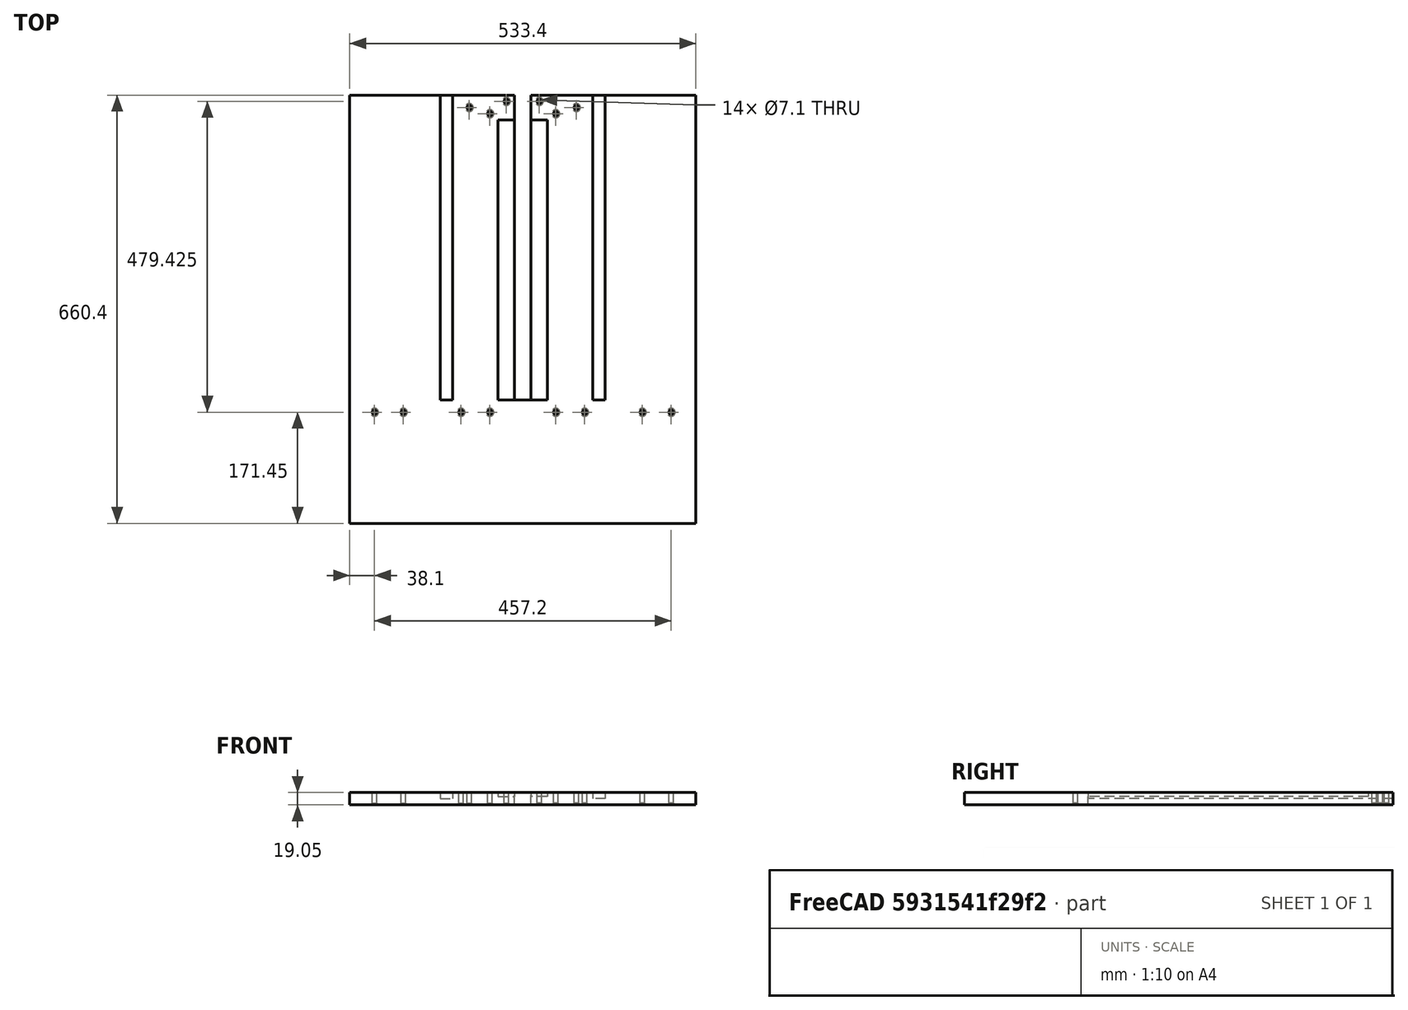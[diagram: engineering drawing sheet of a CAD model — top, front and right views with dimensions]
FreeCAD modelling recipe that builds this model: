
FCSTD DOCUMENT  (FreeCAD 0.20R29603 (Git))
Label: base
License: All rights reserved
LicenseURL: http://en.wikipedia.org/wiki/All_rights_reserved
objects: TechDraw::DrawViewDimension×20, Sketcher::SketchObject×4, PartDesign::Pocket×2, TechDraw::DrawViewPart×2, PartDesign::Pad×1, PartDesign::Hole×1, PartDesign::Mirrored×1, PartDesign::Body×1, TechDraw::DrawSVGTemplate×1, TechDraw::DrawPage×1
note: 14 computed .brp shape members not serialized (recipe doc carries the construction recipe); baked Part::Feature solids carry a one-line shape summary decoded from their .brp

FEATURE [Sketcher::SketchObject] Sketch
  FullyConstrained = true
  MapMode = 5
  Support = -> [XY_Plane]
  sketch-geometry (7):
    g0: LineSegment StartX=-127 StartY=-330.2 StartZ=0 EndX=-127 EndY=330.2 EndZ=0
    g1: LineSegment StartX=-127 StartY=330.2 StartZ=0 EndX=127 EndY=330.2 EndZ=0
    g2: LineSegment StartX=127 StartY=330.2 StartZ=0 EndX=127 EndY=-139.7 EndZ=0
    g3: GeomPoint X=0 Y=0 Z=0
    g4: LineSegment StartX=127 StartY=-139.7 StartZ=0 EndX=139.7 EndY=-139.7 EndZ=0
    g5: LineSegment StartX=139.7 StartY=-139.7 StartZ=0 EndX=139.7 EndY=-330.2 EndZ=0
    g6: LineSegment StartX=-127 StartY=-330.2 StartZ=0 EndX=139.7 EndY=-330.2 EndZ=0
  constraints (18):
    c: Coincident(g0,g1)
    c: Coincident(g1,g2)
    c: Horizontal(g1)
    c: Vertical(g0)
    c: Vertical(g2)
    c: Symmetric(g1,g0,g3)
    c: Coincident(g-1,g3)
    c: DistanceY(g5,g2) = 660.4
    c: DistanceX(g1,g1) = 254
    c: Coincident(g4,g5)
    c: Horizontal(g4)
    c: Vertical(g5)
    c: Distance(g4) = 12.7
    c: Distance(g5) = 190.5
    c: Coincident(g4,g2)
    c: Coincident(g0,g6)
    c: Coincident(g5,g6)
    c: Horizontal(g6)
FEATURE [PartDesign::Pad] Pad
  Direction = (0,0,1)
  Length = 19.05
  Length2 = 10
  Profile = -> Sketch
  ReferenceAxis = -> Sketch [N_Axis]
  Type = 0
FEATURE [Sketcher::SketchObject] Sketch002
  FullyConstrained = false
  MapMode = 5
  Placement = pos=(0,0,19.05) rot=(0,0,1;0rad)
  sketch-geometry (5):
    g0: LineSegment StartX=12.7 StartY=-139.7 StartZ=0 EndX=12.7 EndY=330.2 EndZ=0
    g1: LineSegment StartX=12.7 StartY=330.2 StartZ=0 EndX=31.75 EndY=330.2 EndZ=0
    g2: LineSegment StartX=31.75 StartY=330.2 StartZ=0 EndX=31.75 EndY=-139.7 EndZ=0
    g3: LineSegment StartX=31.75 StartY=-139.7 StartZ=0 EndX=12.7 EndY=-139.7 EndZ=0
    g4: GeomPoint X=22.225 Y=95.25 Z=0
  constraints (8):
    c: Coincident(g0,g1)
    c: Coincident(g1,g2)
    c: Coincident(g2,g3)
    c: Coincident(g3,g0)
    c: Vertical(g0)
    c: Vertical(g2)
    c: Symmetric(g1,g0,g4)
    c: Distance(g3) = 19.05
FEATURE [PartDesign::Pocket] Pocket001
  BaseFeature = -> Pad
  Direction = (0,0,-1)
  Length = 9.525
  Length2 = 5
  Profile = -> Sketch002
  ReferenceAxis = -> Sketch002 [N_Axis]
  Type = 0
FEATURE [Sketcher::SketchObject] Sketch004
  ExternalGeometry = -> [Pocket001]
  FullyConstrained = true
  MapMode = 5
  Placement = pos=(0,0,0) rot=(1,0,0;3.14159rad)
  Support = -> [Pocket001]
  sketch-geometry (7):
    g0: Circle CenterX=-88.9 CenterY=158.75 CenterZ=0 NormalX=0 NormalY=0 NormalZ=1 AngleXU=0 Radius=3.175
    g1: Circle CenterX=88.9 CenterY=158.75 CenterZ=0 NormalX=0 NormalY=0 NormalZ=1 AngleXU=0 Radius=3.175
    g2: Circle CenterX=-44.45 CenterY=158.75 CenterZ=0 NormalX=0 NormalY=0 NormalZ=1 AngleXU=0 Radius=3.175
    g3: Circle CenterX=44.45 CenterY=158.75 CenterZ=0 NormalX=0 NormalY=0 NormalZ=1 AngleXU=0 Radius=3.175
    g4: Circle CenterX=57.15 CenterY=-311.15 CenterZ=0 NormalX=0 NormalY=0 NormalZ=1 AngleXU=0 Radius=3.175
    g5: Circle CenterX=88.9 CenterY=-301.625 CenterZ=0 NormalX=0 NormalY=0 NormalZ=1 AngleXU=0 Radius=3.175
    g6: Circle CenterX=114.3 CenterY=-320.675 CenterZ=0 NormalX=0 NormalY=0 NormalZ=1 AngleXU=0 Radius=3.175
  constraints (19):
    c: Diameter(g0) = 6.35
    c: Distance(g0,g-6) = 38.1
    c: Diameter(g1) = 6.35
    c: Symmetric(g0,g1,g-2)
    c: Equal(g0,g2) = 6.35
    c: Distance(g2,g-2) = 44.45
    c: Horizontal(g0,g2)
    c: Symmetric(g2,g3,g-2)
    c: Equal(g3,g0)
    c: Distance(g4,g-6) = 184.15
    c: Distance(g5,g-6) = 215.9
    c: Distance(g6,g-6) = 241.3
    c: Distance(g6,g-4) = 9.525
    c: Distance(g5,g-4) = 28.575
    c: Distance(g4,g-4) = 19.05
    c: Diameter(g4) = 6.35
    c: Equal(g4,g5)
    c: Equal(g4,g6)
    c: Distance(g2,g-8) = 171.45
FEATURE [PartDesign::Hole] Hole
  BaseFeature = -> Pocket001
  CustomThreadClearance = 0
  Depth = 1147.93
  DepthType = 1
  Diameter = 7.1
  DrillForDepth = false
  DrillPoint = 1
  DrillPointAngle = 118
  HoleCutCountersinkAngle = 82
  HoleCutCustomValues = false
  HoleCutDepth = 0
  HoleCutDiameter = 12.07
  HoleCutType = 2
  ModelThread = false
  Profile = -> Sketch004
  Tapered = false
  TaperedAngle = 90
  ThreadClass = 0
  ThreadDepth = 1147.93
  ThreadDepthType = 0
  ThreadDirection = 0
  ThreadFit = 0
  ThreadSize = 9
  ThreadType = 3
  Threaded = false
  UseCustomThreadClearance = false
FEATURE [Sketcher::SketchObject] Sketch005
  ExternalGeometry = -> [Hole]
  FullyConstrained = true
  MapMode = 5
  Placement = pos=(0,0,19.05) rot=(0,0,1;0rad)
  Support = -> [Hole]
  sketch-geometry (4):
    g0: LineSegment StartX=127 StartY=-139.7 StartZ=0 EndX=101.6 EndY=-139.7 EndZ=0
    g1: LineSegment StartX=101.6 StartY=-139.7 StartZ=0 EndX=101.6 EndY=292.1 EndZ=0
    g2: LineSegment StartX=101.6 StartY=292.1 StartZ=0 EndX=127 EndY=292.1 EndZ=0
    g3: LineSegment StartX=127 StartY=292.1 StartZ=0 EndX=127 EndY=-139.7 EndZ=0
  constraints (10):
    c: Coincident(g0,g1)
    c: Coincident(g1,g2)
    c: Coincident(g2,g3)
    c: Coincident(g3,g0)
    c: Horizontal(g2)
    c: Vertical(g1)
    c: Tangent(g0,g-3)
    c: Tangent(g3,g-4)
    c: Distance(g2) = 25.4
    c: Distance(g2,g-5) = 38.1
FEATURE [PartDesign::Pocket] Pocket
  BaseFeature = -> Hole
  Direction = (0,0,-1)
  Length = 6.35
  Length2 = 5
  Profile = -> Sketch005
  ReferenceAxis = -> Sketch005 [N_Axis]
  Type = 0
FEATURE [PartDesign::Mirrored] Mirrored
  AttacherType = Attacher::AttachEngine3D
  BaseFeature = -> Pocket
  MirrorPlane = -> Pocket [Face6]
  Originals = -> [Pad,Pocket001,Hole,Pocket]
  Refine = true
FEATURE [PartDesign::Body] Body
  Group = -> [Sketch,Pad,Sketch002,Pocket001,Sketch004,Hole,Sketch005,Pocket,Mirrored]
  Origin = -> Origin
  Tip = -> Mirrored
FEATURE [TechDraw::DrawSVGTemplate] Template
  Height = 297
  Orientation = 1
  Width = 420
FEATURE [TechDraw::DrawViewPart] View
  CoarseView = false
  Direction = (0,0,1)
  Focus = 100
  HardHidden = false
  IsoCount = 0
  IsoHidden = false
  IsoVisible = false
  LockPosition = false
  Perspective = false
  Rotation = 90
  Scale = 0.3
  ScaleType = 0
  SeamHidden = false
  SeamVisible = true
  SmoothHidden = false
  SmoothVisible = true
  Source = -> [Body]
  X = 237.237
  XDirection = (1,0,0)
  Y = 178.171
FEATURE [TechDraw::DrawViewDimension] Dimension004
  AngleOverride = false
  Arbitrary = false
  ArbitraryTolerances = false
  EqualTolerance = true
  ExtensionAngle = 0
  FormatSpec = %.2w
  FormatSpecOverTolerance = %+.2w
  FormatSpecUnderTolerance = %+.2w
  Inverted = false
  LineAngle = 0
  LockPosition = false
  MeasureType = 1
  OverTolerance = 0
  References2D = -> [View]
  Rotation = 0
  Scale = 0.3
  ScaleType = 0
  TheoreticalExact = false
  Type = 2
  UnderTolerance = 0
  X = 132.953
  Y = -46.3869
FEATURE [TechDraw::DrawViewDimension] Dimension005
  AngleOverride = false
  Arbitrary = false
  ArbitraryTolerances = false
  EqualTolerance = true
  ExtensionAngle = 0
  FormatSpec = %.2w
  FormatSpecOverTolerance = %+.2w
  FormatSpecUnderTolerance = %+.2w
  Inverted = false
  LineAngle = 0
  LockPosition = false
  MeasureType = 1
  OverTolerance = 0
  References2D = -> [View]
  Rotation = 0
  Scale = 0.3
  ScaleType = 0
  TheoreticalExact = false
  Type = 2
  UnderTolerance = 0
  X = 143.227
  Y = -33.9354
FEATURE [TechDraw::DrawViewDimension] Dimension002
  AngleOverride = false
  Arbitrary = false
  ArbitraryTolerances = false
  EqualTolerance = true
  ExtensionAngle = 0
  FormatSpec = %.2w
  FormatSpecOverTolerance = %+.2w
  FormatSpecUnderTolerance = %+.2w
  Inverted = false
  LineAngle = 0
  LockPosition = false
  MeasureType = 1
  OverTolerance = 0
  References2D = -> [View]
  Rotation = 0
  Scale = 0.3
  ScaleType = 0
  TheoreticalExact = false
  Type = 2
  UnderTolerance = 0
  X = 110.743
  Y = -71.7009
FEATURE [TechDraw::DrawViewDimension] Dimension
  AngleOverride = false
  Arbitrary = false
  ArbitraryTolerances = false
  EqualTolerance = true
  ExtensionAngle = 0
  FormatSpec = %.2w
  FormatSpecOverTolerance = %+.2w
  FormatSpecUnderTolerance = %+.2w
  Inverted = false
  LineAngle = 0
  LockPosition = false
  MeasureType = 1
  OverTolerance = 0
  References2D = -> [View]
  Rotation = 0
  Scale = 0.3
  ScaleType = 0
  TheoreticalExact = false
  Type = 1
  UnderTolerance = 0
  X = 10.2677
  Y = -89.6707
FEATURE [TechDraw::DrawViewDimension] Dimension001
  AngleOverride = false
  Arbitrary = false
  ArbitraryTolerances = false
  EqualTolerance = true
  ExtensionAngle = 0
  FormatSpec = %.2w
  FormatSpecOverTolerance = %+.2w
  FormatSpecUnderTolerance = %+.2w
  Inverted = false
  LineAngle = 0
  LockPosition = false
  MeasureType = 1
  OverTolerance = 0
  References2D = -> [View]
  Rotation = 0
  Scale = 0.3
  ScaleType = 0
  TheoreticalExact = false
  Type = 2
  UnderTolerance = 0
  X = 157.004
  Y = -19.8727
FEATURE [TechDraw::DrawViewDimension] Dimension003
  AngleOverride = false
  Arbitrary = false
  ArbitraryTolerances = false
  EqualTolerance = true
  ExtensionAngle = 0
  FormatSpec = %.2w
  FormatSpecOverTolerance = %+.2w
  FormatSpecUnderTolerance = %+.2w
  Inverted = false
  LineAngle = 0
  LockPosition = false
  MeasureType = 1
  OverTolerance = 0
  References2D = -> [View]
  Rotation = 0
  Scale = 0.3
  ScaleType = 0
  TheoreticalExact = false
  Type = 2
  UnderTolerance = 0
  X = 120.93
  Y = -63.6564
FEATURE [TechDraw::DrawViewDimension] Dimension006
  AngleOverride = false
  Arbitrary = false
  ArbitraryTolerances = false
  EqualTolerance = true
  ExtensionAngle = 0
  FormatSpec = %.2w
  FormatSpecOverTolerance = %+.2w
  FormatSpecUnderTolerance = %+.2w
  Inverted = false
  LineAngle = 0
  LockPosition = false
  MeasureType = 1
  OverTolerance = 0
  References2D = -> [View]
  Rotation = 0
  Scale = 0.3
  ScaleType = 0
  TheoreticalExact = false
  Type = 2
  UnderTolerance = 0
  X = -107.472
  Y = -59.9075
FEATURE [TechDraw::DrawViewDimension] Dimension007
  AngleOverride = false
  Arbitrary = false
  ArbitraryTolerances = false
  EqualTolerance = true
  ExtensionAngle = 0
  FormatSpec = %.2w
  FormatSpecOverTolerance = %+.2w
  FormatSpecUnderTolerance = %+.2w
  Inverted = false
  LineAngle = 0
  LockPosition = false
  MeasureType = 1
  OverTolerance = 0
  References2D = -> [View]
  Rotation = 0
  Scale = 0.3
  ScaleType = 0
  TheoreticalExact = false
  Type = 2
  UnderTolerance = 0
  X = -25.693
  Y = -47.8842
FEATURE [TechDraw::DrawViewDimension] Dimension008
  AngleOverride = false
  Arbitrary = false
  ArbitraryTolerances = false
  EqualTolerance = true
  ExtensionAngle = 0
  FormatSpec = %.2w
  FormatSpecOverTolerance = %+.2w
  FormatSpecUnderTolerance = %+.2w
  Inverted = false
  LineAngle = 0
  LockPosition = false
  MeasureType = 1
  OverTolerance = 0
  References2D = -> [View]
  Rotation = 0
  Scale = 0.3
  ScaleType = 0
  TheoreticalExact = false
  Type = 1
  UnderTolerance = 0
  X = -2.90759
  Y = -52.7167
FEATURE [TechDraw::DrawViewDimension] Dimension012
  AngleOverride = false
  Arbitrary = false
  ArbitraryTolerances = false
  EqualTolerance = true
  ExtensionAngle = 0
  FormatSpec = %.2w
  FormatSpecOverTolerance = %+.2w
  FormatSpecUnderTolerance = %+.2w
  Inverted = false
  LineAngle = 0
  LockPosition = false
  MeasureType = 1
  OverTolerance = 0
  References2D = -> [View]
  Rotation = 0
  Scale = 0.3
  ScaleType = 0
  TheoreticalExact = false
  Type = 1
  UnderTolerance = 0
  X = 30.61
  Y = -83.8092
FEATURE [TechDraw::DrawViewDimension] Dimension013
  AngleOverride = false
  Arbitrary = false
  ArbitraryTolerances = false
  EqualTolerance = true
  ExtensionAngle = 0
  FormatSpec = %.2w
  FormatSpecOverTolerance = %+.2w
  FormatSpecUnderTolerance = %+.2w
  Inverted = false
  LineAngle = 0
  LockPosition = false
  MeasureType = 1
  OverTolerance = 0
  References2D = -> [View]
  Rotation = 0
  Scale = 0.3
  ScaleType = 0
  TheoreticalExact = false
  Type = 1
  UnderTolerance = 0
  X = -124.929
  Y = 12.544
FEATURE [TechDraw::DrawViewDimension] Dimension014
  AngleOverride = false
  Arbitrary = false
  ArbitraryTolerances = false
  EqualTolerance = true
  ExtensionAngle = 0
  FormatSpec = %.2w
  FormatSpecOverTolerance = %+.2w
  FormatSpecUnderTolerance = %+.2w
  Inverted = false
  LineAngle = 0
  LockPosition = false
  MeasureType = 1
  OverTolerance = 0
  References2D = -> [View]
  Rotation = 0
  Scale = 0.3
  ScaleType = 0
  TheoreticalExact = false
  Type = 1
  UnderTolerance = 0
  X = -130.286
  Y = 20.344
FEATURE [TechDraw::DrawViewDimension] Dimension015
  AngleOverride = false
  Arbitrary = false
  ArbitraryTolerances = false
  EqualTolerance = true
  ExtensionAngle = 0
  FormatSpec = %.2w
  FormatSpecOverTolerance = %+.2w
  FormatSpecUnderTolerance = %+.2w
  Inverted = false
  LineAngle = 0
  LockPosition = false
  MeasureType = 1
  OverTolerance = 0
  References2D = -> [View]
  Rotation = 0
  Scale = 0.3
  ScaleType = 0
  TheoreticalExact = false
  Type = 0
  UnderTolerance = 0
  X = -130.265
  Y = 29.8655
FEATURE [TechDraw::DrawViewDimension] Dimension016
  AngleOverride = false
  Arbitrary = false
  ArbitraryTolerances = false
  EqualTolerance = true
  ExtensionAngle = 0
  FormatSpec = %.2w
  FormatSpecOverTolerance = %+.2w
  FormatSpecUnderTolerance = %+.2w
  Inverted = false
  LineAngle = 0
  LockPosition = false
  MeasureType = 1
  OverTolerance = 0
  References2D = -> [View]
  Rotation = 0
  Scale = 0.3
  ScaleType = 0
  TheoreticalExact = false
  Type = 1
  UnderTolerance = 0
  X = -71.8932
  Y = -26.5704
FEATURE [TechDraw::DrawViewDimension] Dimension017
  AngleOverride = false
  Arbitrary = false
  ArbitraryTolerances = false
  EqualTolerance = true
  ExtensionAngle = 0
  FormatSpec = %.2w
  FormatSpecOverTolerance = %+.2w
  FormatSpecUnderTolerance = %+.2w
  Inverted = false
  LineAngle = 0
  LockPosition = false
  MeasureType = 1
  OverTolerance = 0
  References2D = -> [View]
  Rotation = 0
  Scale = 0.3
  ScaleType = 0
  TheoreticalExact = false
  Type = 1
  UnderTolerance = 0
  X = -4.20716
  Y = -14.7418
FEATURE [TechDraw::DrawViewDimension] Dimension018
  AngleOverride = false
  Arbitrary = false
  ArbitraryTolerances = false
  EqualTolerance = true
  ExtensionAngle = 0
  FormatSpec = %.2w
  FormatSpecOverTolerance = %+.2w
  FormatSpecUnderTolerance = %+.2w
  Inverted = false
  LineAngle = 0
  LockPosition = false
  MeasureType = 1
  OverTolerance = 0
  References2D = -> [View]
  Rotation = 0
  Scale = 0.3
  ScaleType = 0
  TheoreticalExact = false
  Type = 2
  UnderTolerance = 0
  X = 48.2145
  Y = -6.02509
FEATURE [TechDraw::DrawViewPart] View001
  CoarseView = false
  Direction = (0,1,0)
  Focus = 100
  HardHidden = false
  IsoCount = 0
  IsoHidden = false
  IsoVisible = false
  LockPosition = false
  Perspective = false
  Rotation = 90
  Scale = 0.3
  ScaleType = 0
  SeamHidden = false
  SeamVisible = true
  SmoothHidden = false
  SmoothVisible = true
  Source = -> [Body]
  X = 55.9529
  XDirection = (-1,0,0)
  Y = 176.458
FEATURE [TechDraw::DrawViewDimension] Dimension019
  AngleOverride = false
  Arbitrary = false
  ArbitraryTolerances = false
  EqualTolerance = true
  ExtensionAngle = 0
  FormatSpec = %.2w
  FormatSpecOverTolerance = %+.2w
  FormatSpecUnderTolerance = %+.2w
  Inverted = false
  LineAngle = 0
  LockPosition = false
  MeasureType = 1
  OverTolerance = 0
  References2D = -> [View001]
  Rotation = 0
  Scale = 0.3
  ScaleType = 0
  TheoreticalExact = false
  Type = 1
  UnderTolerance = 0
  X = 19.7181
  Y = 86.8041
FEATURE [TechDraw::DrawViewDimension] Dimension020
  AngleOverride = false
  Arbitrary = false
  ArbitraryTolerances = false
  EqualTolerance = true
  ExtensionAngle = 0
  FormatSpec = %.2w
  FormatSpecOverTolerance = %+.2w
  FormatSpecUnderTolerance = %+.2w
  Inverted = false
  LineAngle = 0
  LockPosition = false
  MeasureType = 1
  OverTolerance = 0
  References2D = -> [View001]
  Rotation = 0
  Scale = 0.3
  ScaleType = 0
  TheoreticalExact = false
  Type = 0
  UnderTolerance = 0
  X = -12.2844
  Y = 26.5389
FEATURE [TechDraw::DrawViewDimension] Dimension021
  AngleOverride = false
  Arbitrary = false
  ArbitraryTolerances = false
  EqualTolerance = true
  ExtensionAngle = 0
  FormatSpec = %.2w
  FormatSpecOverTolerance = %+.2w
  FormatSpecUnderTolerance = %+.2w
  Inverted = false
  LineAngle = 0
  LockPosition = false
  MeasureType = 1
  OverTolerance = 0
  References2D = -> [View001]
  Rotation = 0
  Scale = 0.3
  ScaleType = 0
  TheoreticalExact = false
  Type = 0
  UnderTolerance = 0
  X = -10.9526
  Y = -14.0394
FEATURE [TechDraw::DrawViewDimension] Dimension022
  AngleOverride = false
  Arbitrary = false
  ArbitraryTolerances = false
  EqualTolerance = true
  ExtensionAngle = 0
  FormatSpec = ⌀%.2w 14x
  FormatSpecOverTolerance = %+.2w
  FormatSpecUnderTolerance = %+.2w
  Inverted = false
  LineAngle = 0
  LockPosition = false
  MeasureType = 1
  OverTolerance = 0
  References2D = -> [View]
  Rotation = 0
  Scale = 0.3
  ScaleType = 0
  TheoreticalExact = false
  Type = 5
  UnderTolerance = 0
  X = 76.2175
  Y = 50.6059
FEATURE [TechDraw::DrawPage] Page
  KeepUpdated = true
  NextBalloonIndex = 1
  ProjectionType = 0
  Scale = 0.3
  Template = -> Template
  Views = -> [View,Dimension,Dimension001,Dimension002,Dimension003,Dimension004,Dimension005,Dimension006,Dimension007,Dimension008,Dimension012,Dimension013,Dimension014,Dimension015,Dimension016,Dimension017,Dimension018,View001,Dimension019,Dimension020,Dimension021,Dimension022]
